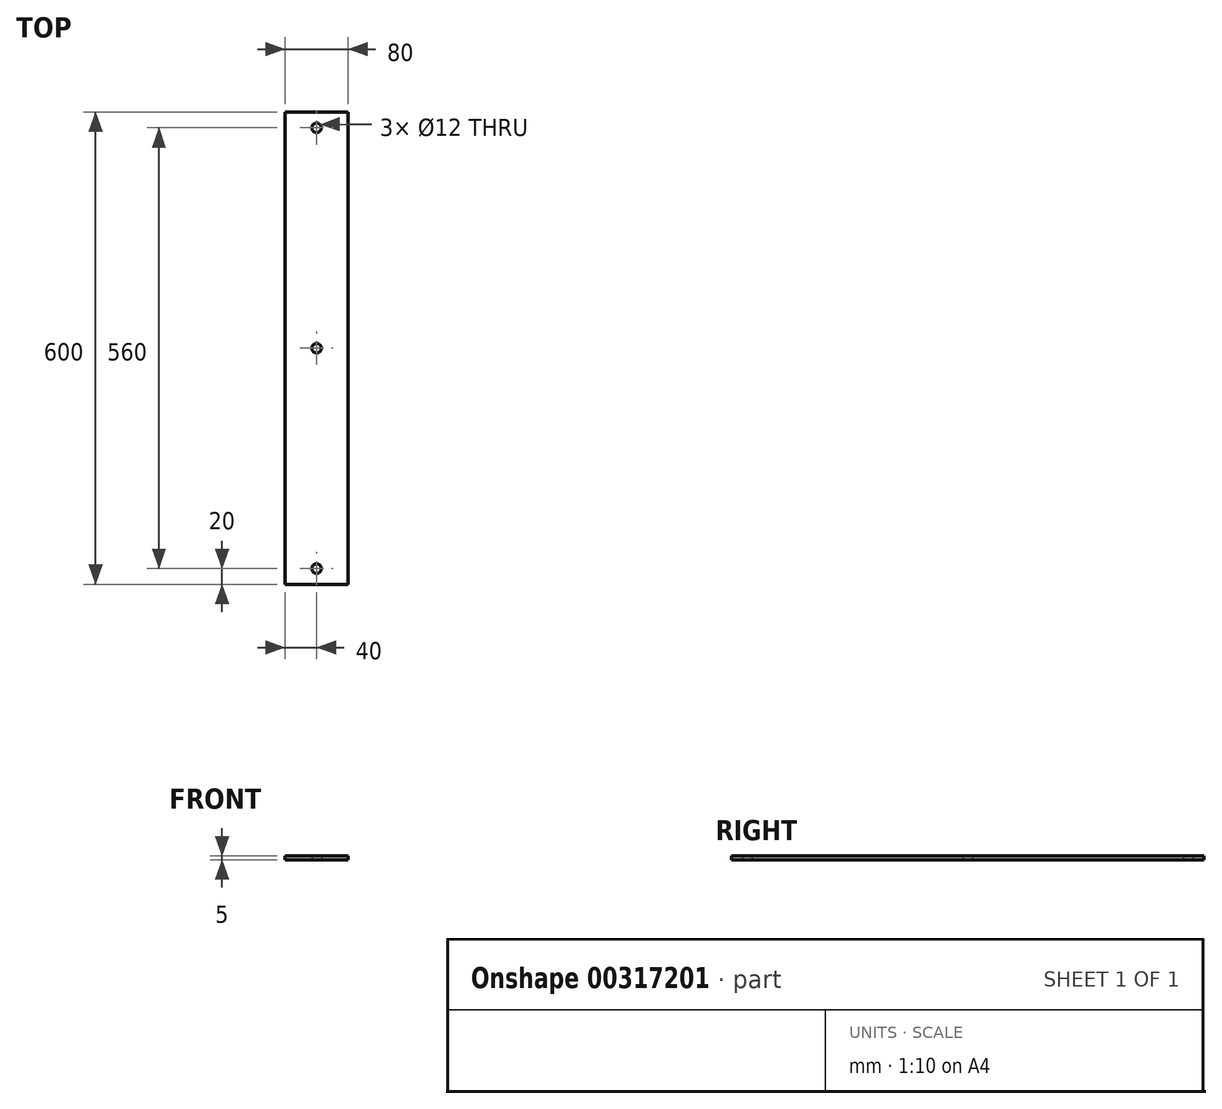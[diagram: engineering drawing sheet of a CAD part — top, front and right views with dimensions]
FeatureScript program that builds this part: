
annotation { "Feature Type Name" : "Feature", "Feature Type Description" : "" }
export const myFeature = defineFeature(function(context is Context, id is Id, definition is map)
    precondition{}
    {
        {
            var Q0;
            Q0=qCreatedBy(makeId("Top.planeOp"),FACE);
            var sketch = newSketch(context, id + "F0", { "sketchPlane" : qUnion([Q0])});
            skLineSegment(sketch, "E0.bottom", {"start": v(-40, 300) * mm, "end": v(40, 300) * mm});
            skLineSegment(sketch, "E0.top", {"start": v(-40, -300) * mm, "end": v(40, -300) * mm});
            skLineSegment(sketch, "E0.left", {"start": v(-40, 300) * mm, "end": v(-40, -300) * mm});
            skLineSegment(sketch, "E0.right", {"start": v(40, 300) * mm, "end": v(40, -300) * mm});
            skLineSegment(sketch, "E1", {"start": v(-40, 300) * mm, "end": v(40, -300) * mm, "construction": true});
            skSolve(sketch);
        }
        {
            var Q0;
            Q0 = qSketchRegion(id + "F0", true);
            extrude(context, id + "F1", {"entities" : qUnion([Q0]), "depth" : 5 * mm});
        }
        {
            var Q0;
            Q0=qCreatedBy(makeId("Top.planeOp"),FACE);
            var sketch = newSketch(context, id + "F2", { "sketchPlane" : qUnion([Q0])});
            skCircle(sketch, "E2", {"center": v(0, 280) * mm, "radius": 6 * mm});
            skCircle(sketch, "E3", {"center": v(0, 0) * mm, "radius": 6 * mm});
            skCircle(sketch, "E4", {"center": v(0, -280) * mm, "radius": 6 * mm});
            skLineSegment(sketch, "E5", {"start": v(0, 280) * mm, "end": v(0, 0) * mm, "construction": true});
            skLineSegment(sketch, "E6", {"start": v(0, -280) * mm, "end": v(0, 0) * mm, "construction": true});
            skSolve(sketch);
        }
        {
            var Q0;
            Q0 = qSketchRegion(id + "F2", true);
            extrude(context, id + "F3", {"entities" : qUnion([Q0]), "operationType" : NewBodyOperationType.REMOVE, "depth" : 25 * mm});
        }
    });
